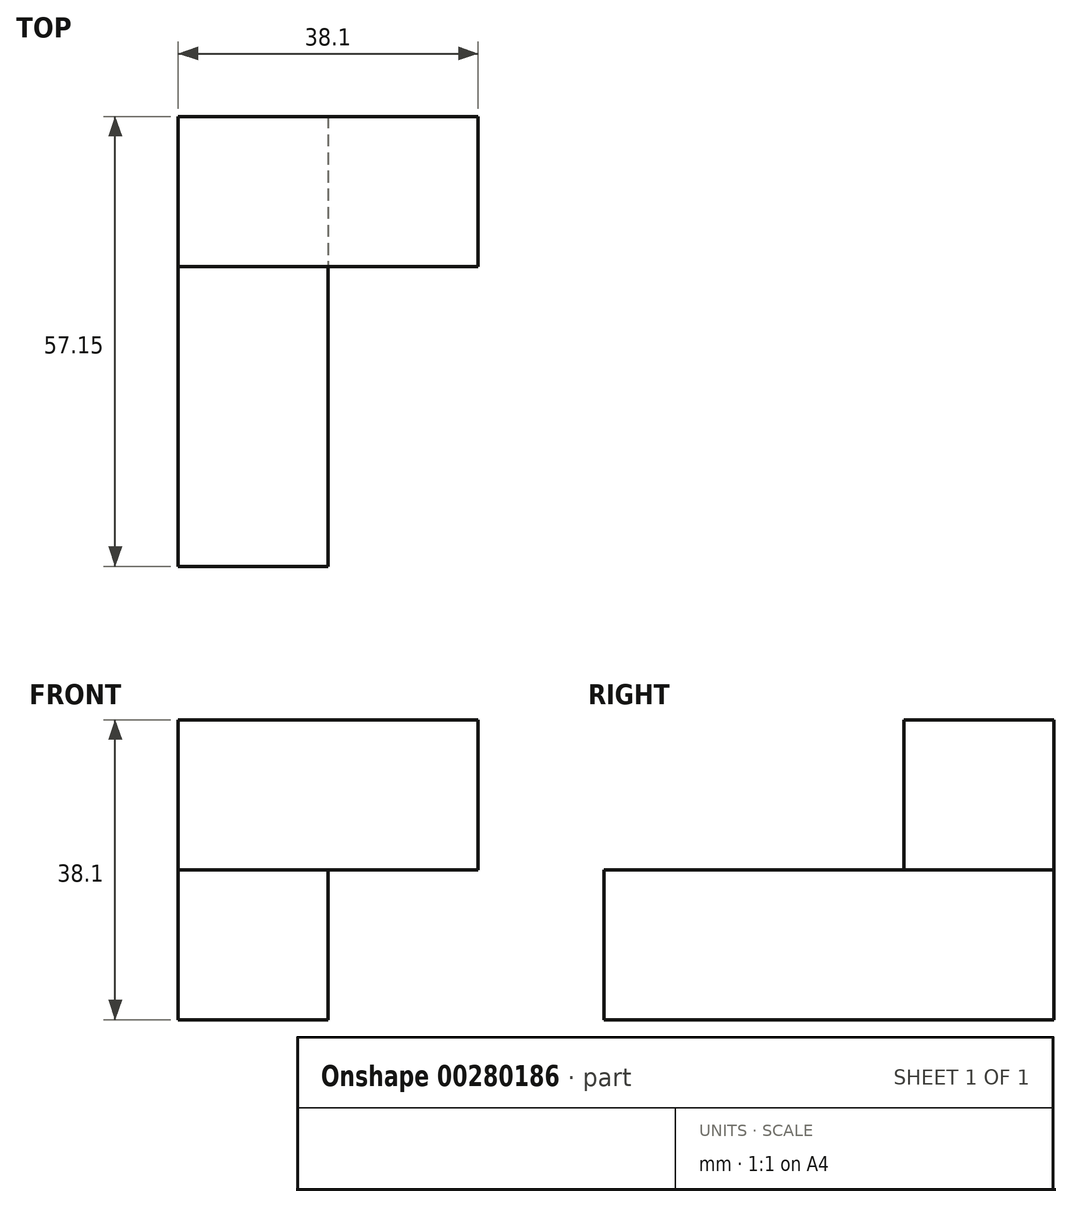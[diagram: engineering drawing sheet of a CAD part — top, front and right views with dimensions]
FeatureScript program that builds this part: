
annotation { "Feature Type Name" : "Feature", "Feature Type Description" : "" }
export const myFeature = defineFeature(function(context is Context, id is Id, definition is map)
    precondition{}
    {
        {
            var Q0;
            Q0=qCreatedBy(makeId("Top.planeOp"),FACE);
            var sketch = newSketch(context, id + "F0", { "sketchPlane" : qUnion([Q0])});
            skLineSegment(sketch, "E0.bottom", {"start": v(0, 0) * mm, "end": v(19.05, 0) * mm});
            skLineSegment(sketch, "E0.top", {"start": v(0, -57.15) * mm, "end": v(19.05, -57.15) * mm});
            skLineSegment(sketch, "E0.left", {"start": v(0, 0) * mm, "end": v(0, -57.15) * mm});
            skLineSegment(sketch, "E0.right", {"start": v(19.05, 0) * mm, "end": v(19.05, -57.15) * mm});
            skSolve(sketch);
        }
        {
            var Q0;
            Q0 = qSketchRegion(id + "F0", true);
            extrude(context, id + "F1", {"entities" : qUnion([Q0]), "depth" : 19.05 * mm});
        }
        {
            var Q0;
            Q0=makeQuery(id+"F1.opExtrude","CAP_FACE",FACE,{"disambiguationData":[OSD([sQuery(id+"F0.wireOp",EDGE,"E0.bottom"),sQuery(id+"F0.wireOp",EDGE,"E0.top"),sQuery(id+"F0.wireOp",EDGE,"E0.left"),sQuery(id+"F0.wireOp",EDGE,"E0.right")])],"isStart":false});
            var sketch = newSketch(context, id + "F2", { "sketchPlane" : qUnion([Q0])});
            skLineSegment(sketch, "E1.bottom", {"start": v(0, 0) * mm, "end": v(19.05, 0) * mm});
            skLineSegment(sketch, "E1.top", {"start": v(0, -19.05) * mm, "end": v(19.05, -19.05) * mm});
            skLineSegment(sketch, "E1.left", {"start": v(0, 0) * mm, "end": v(0, -19.05) * mm});
            skLineSegment(sketch, "E1.right", {"start": v(19.05, 0) * mm, "end": v(19.05, -19.05) * mm});
            skSolve(sketch);
        }
        {
            var Q0;
            Q0 = qSketchRegion(id + "F2", true);
            extrude(context, id + "F3", {"entities" : qUnion([Q0]), "operationType" : NewBodyOperationType.ADD, "depth" : 19.05 * mm});
        }
        {
            var Q0;
            Q0=makeQuery(id+"F3.boolean.opBoolean","MERGE",FACE,{"derivedFrom":[makeQuery(id+"F1.opExtrude","SWEPT_FACE",FACE,{"disambiguationData":[OSD([sQuery(id+"F0.wireOp",EDGE,"E0.right")])]}),makeQuery(id+"F3.opExtrude","SWEPT_FACE",FACE,{"disambiguationData":[OSD([sQuery(id+"F2.wireOp",EDGE,"E1.right")])]})]});
            var sketch = newSketch(context, id + "F4", { "sketchPlane" : qUnion([Q0])});
            skLineSegment(sketch, "E2.bottom", {"start": v(0, 38.1) * mm, "end": v(-19.05, 38.1) * mm});
            skLineSegment(sketch, "E2.top", {"start": v(0, 19.05) * mm, "end": v(-19.05, 19.05) * mm});
            skLineSegment(sketch, "E2.left", {"start": v(0, 38.1) * mm, "end": v(0, 19.05) * mm});
            skLineSegment(sketch, "E2.right", {"start": v(-19.05, 38.1) * mm, "end": v(-19.05, 19.05) * mm});
            skSolve(sketch);
        }
        {
            var Q0;
            Q0 = qSketchRegion(id + "F4", true);
            extrude(context, id + "F5", {"entities" : qUnion([Q0]), "operationType" : NewBodyOperationType.ADD, "depth" : 19.05 * mm});
        }
    });
